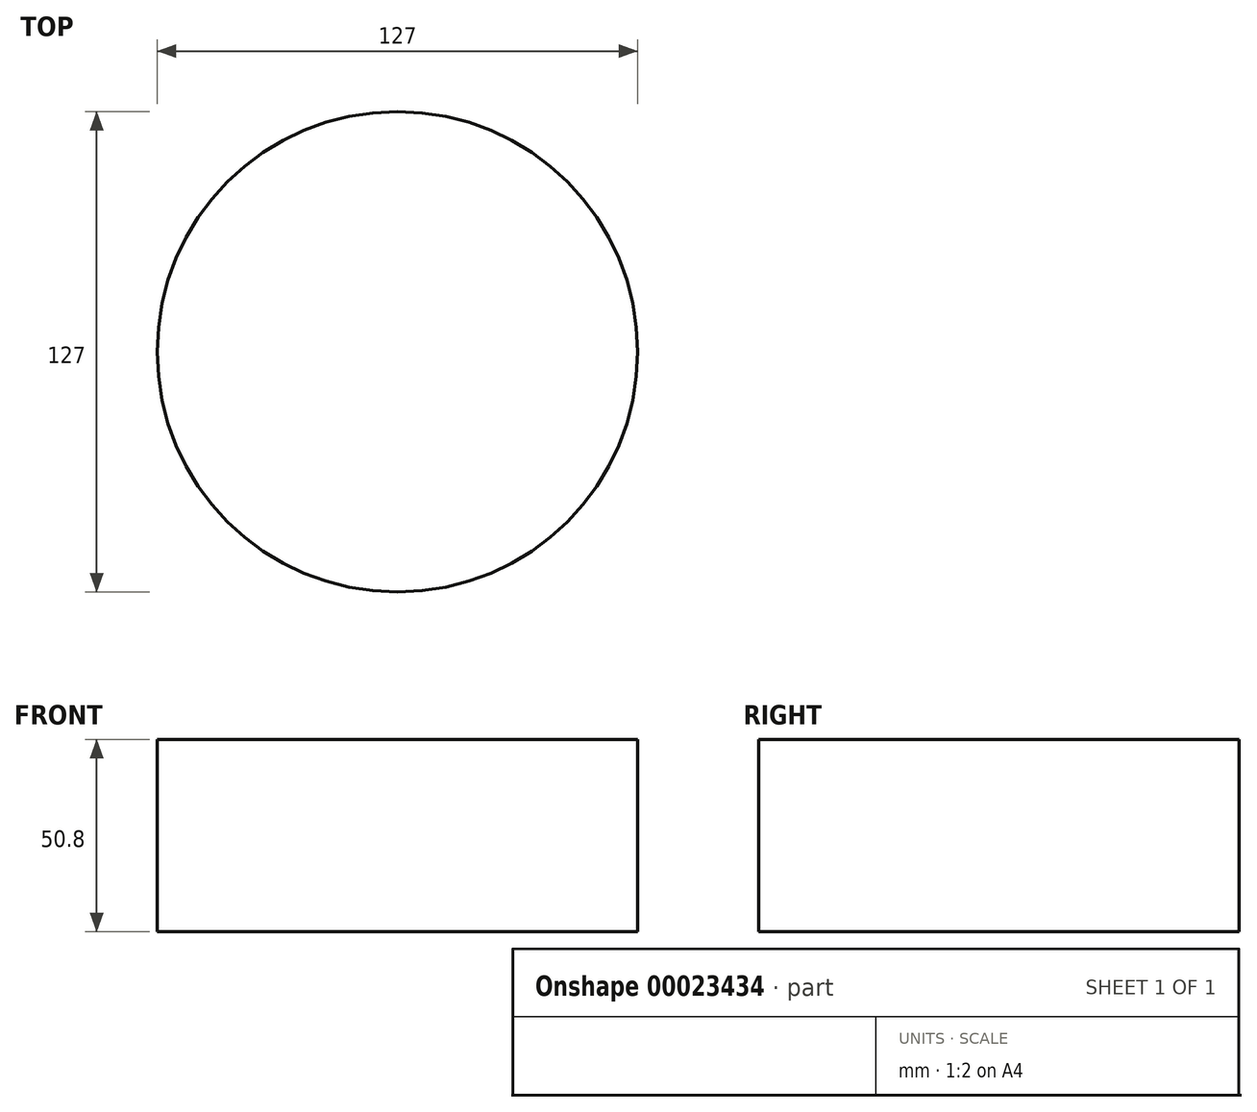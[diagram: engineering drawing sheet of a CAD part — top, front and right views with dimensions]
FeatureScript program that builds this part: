
annotation { "Feature Type Name" : "Feature", "Feature Type Description" : "" }
export const myFeature = defineFeature(function(context is Context, id is Id, definition is map)
    precondition{}
    {
        {
            var Q0;
            Q0=qCreatedBy(makeId("Top.planeOp"),FACE);
            var sketch = newSketch(context, id + "F0", { "sketchPlane" : qUnion([Q0])});
            skCircle(sketch, "E0", {"center": v(0, 0) * mm, "radius": 63.5 * mm});
            skSolve(sketch);
        }
        {
            var Q0;
            Q0 = qSketchRegion(id + "F0", true);
            extrude(context, id + "F1", {"entities" : qUnion([Q0]), "depth" : 50.8 * mm});
        }
    });
